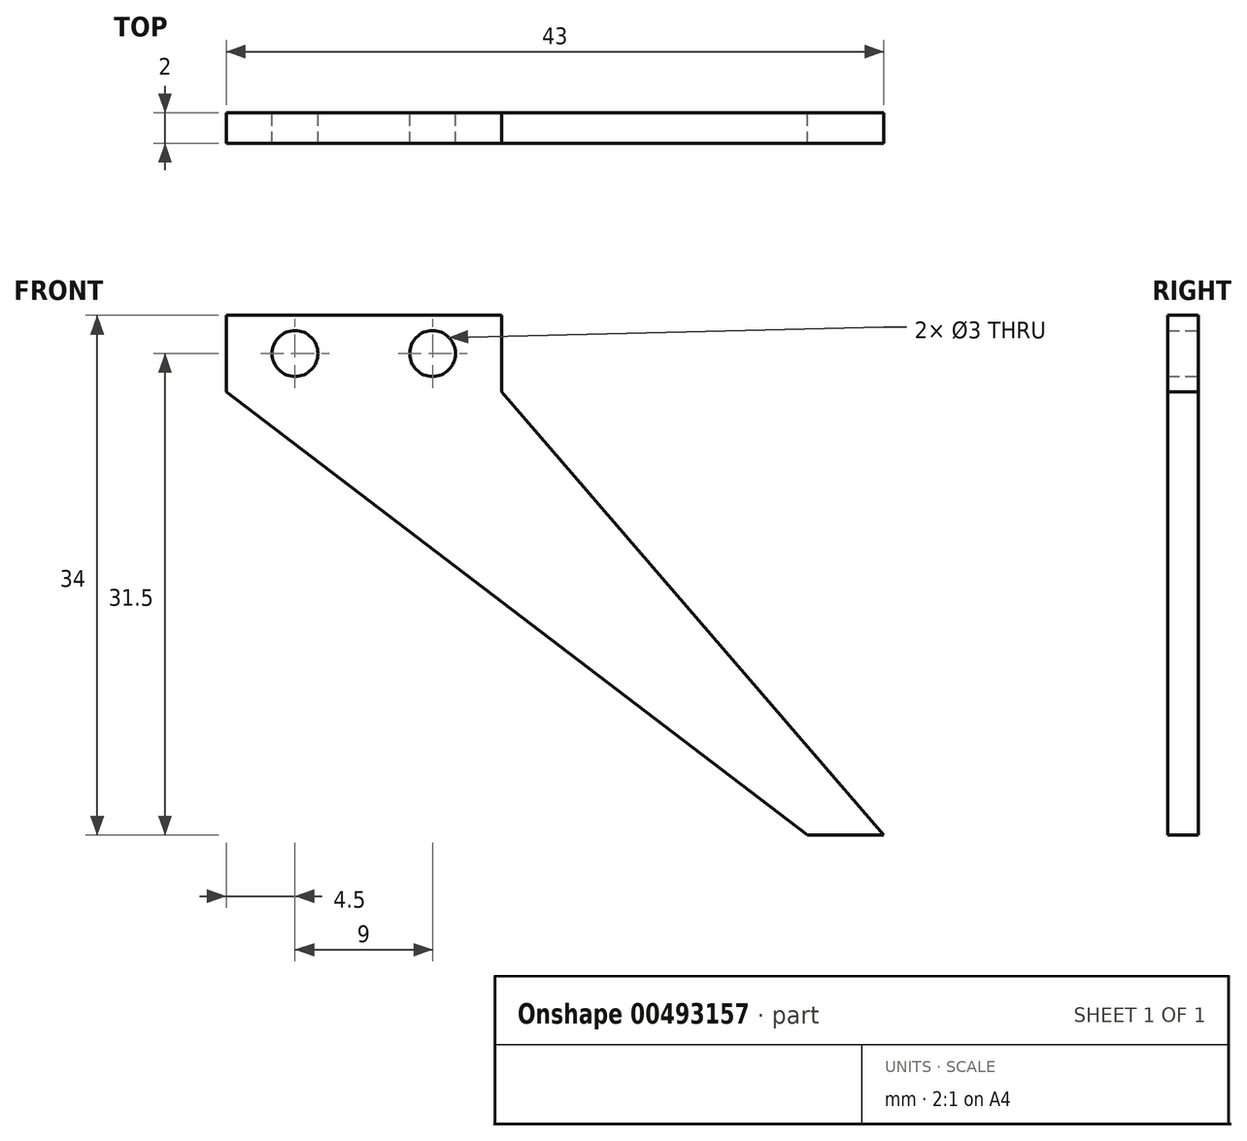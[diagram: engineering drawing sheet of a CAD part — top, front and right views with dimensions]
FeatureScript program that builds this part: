
annotation { "Feature Type Name" : "Feature", "Feature Type Description" : "" }
export const myFeature = defineFeature(function(context is Context, id is Id, definition is map)
    precondition{}
    {
        {
            var Q0;
            Q0=qCreatedBy(makeId("Front.planeOp"),FACE);
            var sketch = newSketch(context, id + "F0", { "sketchPlane" : qUnion([Q0])});
            skLineSegment(sketch, "E0.bottom", {"start": v(9, 2.5) * mm, "end": v(-9, 2.5) * mm});
            skLineSegment(sketch, "E0.top", {"start": v(9, -2.5) * mm, "end": v(-9, -2.5) * mm});
            skLineSegment(sketch, "E0.left", {"start": v(9, 2.5) * mm, "end": v(9, -2.5) * mm});
            skLineSegment(sketch, "E0.right", {"start": v(-9, 2.5) * mm, "end": v(-9, -2.5) * mm});
            skPoint(sketch, "E0.middle", {"position": v(0, 0) * mm});
            skCircle(sketch, "E1", {"center": v(-4.5, 0) * mm, "radius": 1.5 * mm});
            skCircle(sketch, "E2", {"center": v(4.5, 0) * mm, "radius": 1.5 * mm});
            skLineSegment(sketch, "E3", {"start": v(-9, -2.5) * mm, "end": v(29, -31.5) * mm});
            skLineSegment(sketch, "E4", {"start": v(29, -31.5) * mm, "end": v(34, -31.5) * mm});
            skLineSegment(sketch, "E5", {"start": v(34, -31.5) * mm, "end": v(9, -2.5) * mm});
            skSolve(sketch);
        }
        {
            var Q0;
            Q0 = qSketchRegion(id + "F0", true);
            extrude(context, id + "F1", {"entities" : qUnion([Q0]), "depth" : 2 * mm});
        }
    });
